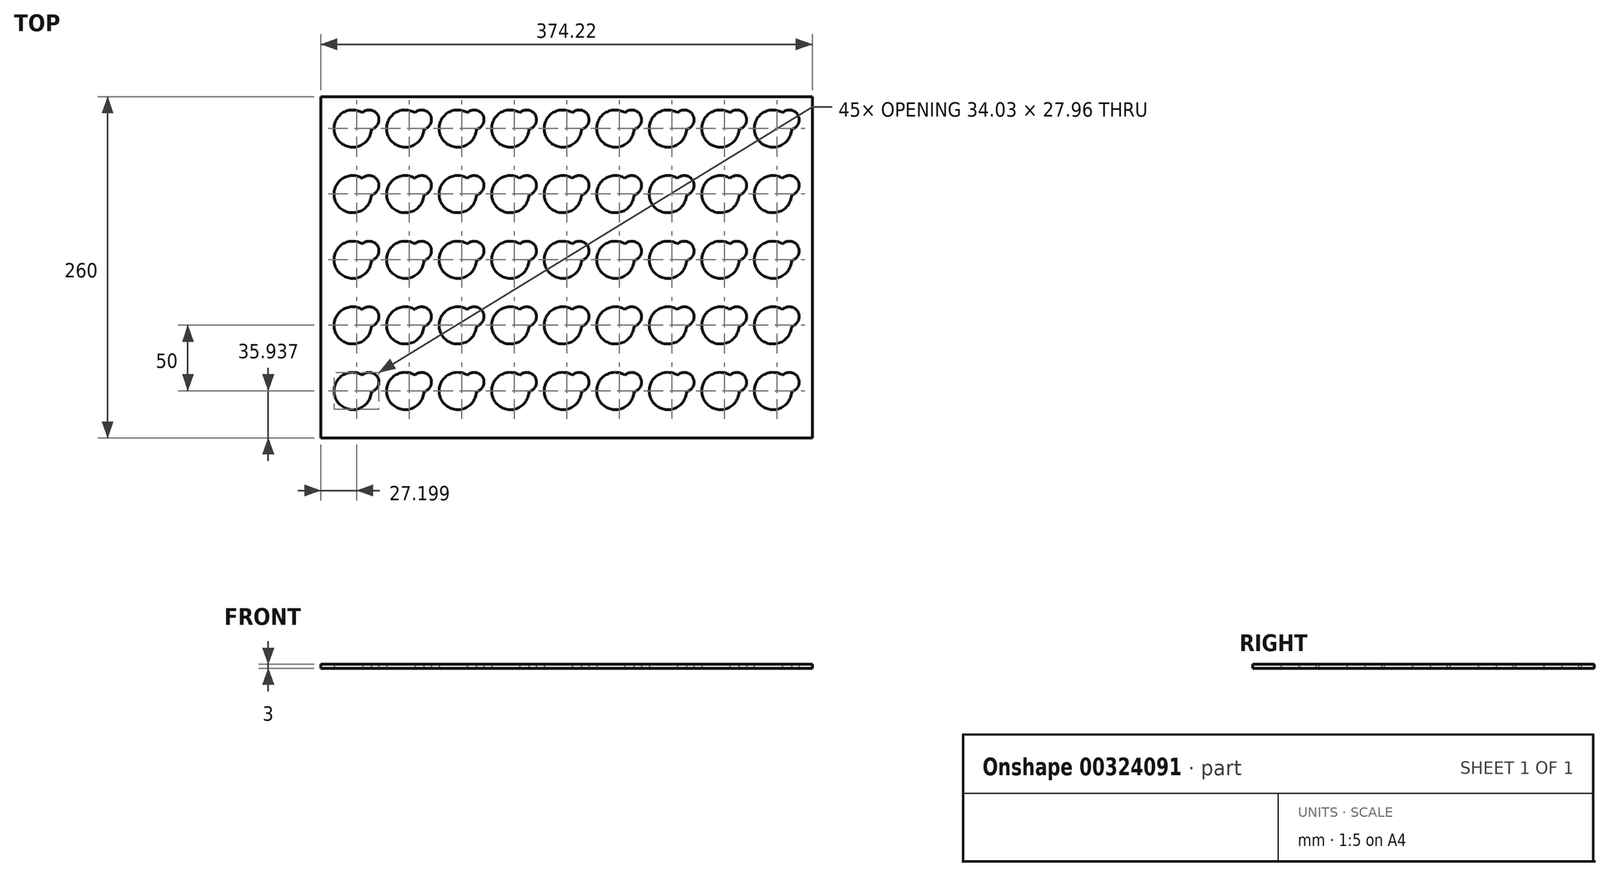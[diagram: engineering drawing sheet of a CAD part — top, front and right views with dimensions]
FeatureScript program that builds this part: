
annotation { "Feature Type Name" : "Feature", "Feature Type Description" : "" }
export const myFeature = defineFeature(function(context is Context, id is Id, definition is map)
    precondition{}
    {
        {
            var Q0;
            Q0=qCreatedBy(makeId("Top.planeOp"),FACE);
            var sketch = newSketch(context, id + "F0", { "sketchPlane" : qUnion([Q0])});
            skArc(sketch, "E0", {"start": v(7.36, 12.14) * mm, "mid": v(-12.52, -6.7) * mm, "end": v(14.19, -0.61) * mm});
            skArc(sketch, "E1", {"start": v(14.19, -0.61) * mm, "mid": v(19.13, 10.24) * mm, "end": v(7.36, 12.14) * mm});
            skLineSegment(sketch, "E2", {"start": v(0, 14.2) * mm, "end": v(12.52, 14.2) * mm, "construction": true});
            skArc(sketch, "E3.0.1.0", {"start": v(7.36, -37.86) * mm, "mid": v(-12.52, -56.7) * mm, "end": v(14.19, -50.61) * mm});
            skArc(sketch, "E3.0.1.1", {"start": v(14.19, -50.61) * mm, "mid": v(19.13, -39.76) * mm, "end": v(7.36, -37.86) * mm});
            skArc(sketch, "E3.0.2.0", {"start": v(7.36, -87.86) * mm, "mid": v(-12.52, -106.7) * mm, "end": v(14.19, -100.61) * mm});
            skArc(sketch, "E3.0.2.1", {"start": v(14.19, -100.61) * mm, "mid": v(19.13, -89.76) * mm, "end": v(7.36, -87.86) * mm});
            skArc(sketch, "E3.0.3.0", {"start": v(7.36, -137.86) * mm, "mid": v(-12.52, -156.7) * mm, "end": v(14.19, -150.61) * mm});
            skArc(sketch, "E3.0.3.1", {"start": v(14.19, -150.61) * mm, "mid": v(19.13, -139.76) * mm, "end": v(7.36, -137.86) * mm});
            skArc(sketch, "E3.0.4.0", {"start": v(7.36, -187.86) * mm, "mid": v(-12.52, -206.7) * mm, "end": v(14.19, -200.61) * mm});
            skArc(sketch, "E3.0.4.1", {"start": v(14.19, -200.61) * mm, "mid": v(19.13, -189.76) * mm, "end": v(7.36, -187.86) * mm});
            skArc(sketch, "E3.1.0.0", {"start": v(47.36, 12.14) * mm, "mid": v(27.48, -6.7) * mm, "end": v(54.19, -0.61) * mm});
            skArc(sketch, "E3.1.0.1", {"start": v(54.19, -0.61) * mm, "mid": v(59.13, 10.24) * mm, "end": v(47.36, 12.14) * mm});
            skArc(sketch, "E3.1.1.0", {"start": v(47.36, -37.86) * mm, "mid": v(27.48, -56.7) * mm, "end": v(54.19, -50.61) * mm});
            skArc(sketch, "E3.1.1.1", {"start": v(54.19, -50.61) * mm, "mid": v(59.13, -39.76) * mm, "end": v(47.36, -37.86) * mm});
            skArc(sketch, "E3.1.2.0", {"start": v(47.36, -87.86) * mm, "mid": v(27.48, -106.7) * mm, "end": v(54.19, -100.61) * mm});
            skArc(sketch, "E3.1.2.1", {"start": v(54.19, -100.61) * mm, "mid": v(59.13, -89.76) * mm, "end": v(47.36, -87.86) * mm});
            skArc(sketch, "E3.1.3.0", {"start": v(47.36, -137.86) * mm, "mid": v(27.48, -156.7) * mm, "end": v(54.19, -150.61) * mm});
            skArc(sketch, "E3.1.3.1", {"start": v(54.19, -150.61) * mm, "mid": v(59.13, -139.76) * mm, "end": v(47.36, -137.86) * mm});
            skArc(sketch, "E3.1.4.0", {"start": v(47.36, -187.86) * mm, "mid": v(27.48, -206.7) * mm, "end": v(54.19, -200.61) * mm});
            skArc(sketch, "E3.1.4.1", {"start": v(54.19, -200.61) * mm, "mid": v(59.13, -189.76) * mm, "end": v(47.36, -187.86) * mm});
            skArc(sketch, "E3.2.0.0", {"start": v(87.36, 12.14) * mm, "mid": v(67.48, -6.7) * mm, "end": v(94.19, -0.61) * mm});
            skArc(sketch, "E3.2.0.1", {"start": v(94.19, -0.61) * mm, "mid": v(99.13, 10.24) * mm, "end": v(87.36, 12.14) * mm});
            skArc(sketch, "E3.2.1.0", {"start": v(87.36, -37.86) * mm, "mid": v(67.48, -56.7) * mm, "end": v(94.19, -50.61) * mm});
            skArc(sketch, "E3.2.1.1", {"start": v(94.19, -50.61) * mm, "mid": v(99.13, -39.76) * mm, "end": v(87.36, -37.86) * mm});
            skArc(sketch, "E3.2.2.0", {"start": v(87.36, -87.86) * mm, "mid": v(67.48, -106.7) * mm, "end": v(94.19, -100.61) * mm});
            skArc(sketch, "E3.2.2.1", {"start": v(94.19, -100.61) * mm, "mid": v(99.13, -89.76) * mm, "end": v(87.36, -87.86) * mm});
            skArc(sketch, "E3.2.3.0", {"start": v(87.36, -137.86) * mm, "mid": v(67.48, -156.7) * mm, "end": v(94.19, -150.61) * mm});
            skArc(sketch, "E3.2.3.1", {"start": v(94.19, -150.61) * mm, "mid": v(99.13, -139.76) * mm, "end": v(87.36, -137.86) * mm});
            skArc(sketch, "E3.2.4.0", {"start": v(87.36, -187.86) * mm, "mid": v(67.48, -206.7) * mm, "end": v(94.19, -200.61) * mm});
            skArc(sketch, "E3.2.4.1", {"start": v(94.19, -200.61) * mm, "mid": v(99.13, -189.76) * mm, "end": v(87.36, -187.86) * mm});
            skArc(sketch, "E3.3.0.0", {"start": v(127.36, 12.14) * mm, "mid": v(107.48, -6.7) * mm, "end": v(134.19, -0.61) * mm});
            skArc(sketch, "E3.3.0.1", {"start": v(134.19, -0.61) * mm, "mid": v(139.13, 10.24) * mm, "end": v(127.36, 12.14) * mm});
            skArc(sketch, "E3.3.1.0", {"start": v(127.36, -37.86) * mm, "mid": v(107.48, -56.7) * mm, "end": v(134.19, -50.61) * mm});
            skArc(sketch, "E3.3.1.1", {"start": v(134.19, -50.61) * mm, "mid": v(139.13, -39.76) * mm, "end": v(127.36, -37.86) * mm});
            skArc(sketch, "E3.3.2.0", {"start": v(127.36, -87.86) * mm, "mid": v(107.48, -106.7) * mm, "end": v(134.19, -100.61) * mm});
            skArc(sketch, "E3.3.2.1", {"start": v(134.19, -100.61) * mm, "mid": v(139.13, -89.76) * mm, "end": v(127.36, -87.86) * mm});
            skArc(sketch, "E3.3.3.0", {"start": v(127.36, -137.86) * mm, "mid": v(107.48, -156.7) * mm, "end": v(134.19, -150.61) * mm});
            skArc(sketch, "E3.3.3.1", {"start": v(134.19, -150.61) * mm, "mid": v(139.13, -139.76) * mm, "end": v(127.36, -137.86) * mm});
            skArc(sketch, "E3.3.4.0", {"start": v(127.36, -187.86) * mm, "mid": v(107.48, -206.7) * mm, "end": v(134.19, -200.61) * mm});
            skArc(sketch, "E3.3.4.1", {"start": v(134.19, -200.61) * mm, "mid": v(139.13, -189.76) * mm, "end": v(127.36, -187.86) * mm});
            skArc(sketch, "E3.4.0.0", {"start": v(167.36, 12.14) * mm, "mid": v(147.48, -6.7) * mm, "end": v(174.19, -0.61) * mm});
            skArc(sketch, "E3.4.0.1", {"start": v(174.19, -0.61) * mm, "mid": v(179.13, 10.24) * mm, "end": v(167.36, 12.14) * mm});
            skArc(sketch, "E3.4.1.0", {"start": v(167.36, -37.86) * mm, "mid": v(147.48, -56.7) * mm, "end": v(174.19, -50.61) * mm});
            skArc(sketch, "E3.4.1.1", {"start": v(174.19, -50.61) * mm, "mid": v(179.13, -39.76) * mm, "end": v(167.36, -37.86) * mm});
            skArc(sketch, "E3.4.2.0", {"start": v(167.36, -87.86) * mm, "mid": v(147.48, -106.7) * mm, "end": v(174.19, -100.61) * mm});
            skArc(sketch, "E3.4.2.1", {"start": v(174.19, -100.61) * mm, "mid": v(179.13, -89.76) * mm, "end": v(167.36, -87.86) * mm});
            skArc(sketch, "E3.4.3.0", {"start": v(167.36, -137.86) * mm, "mid": v(147.48, -156.7) * mm, "end": v(174.19, -150.61) * mm});
            skArc(sketch, "E3.4.3.1", {"start": v(174.19, -150.61) * mm, "mid": v(179.13, -139.76) * mm, "end": v(167.36, -137.86) * mm});
            skArc(sketch, "E3.4.4.0", {"start": v(167.36, -187.86) * mm, "mid": v(147.48, -206.7) * mm, "end": v(174.19, -200.61) * mm});
            skArc(sketch, "E3.4.4.1", {"start": v(174.19, -200.61) * mm, "mid": v(179.13, -189.76) * mm, "end": v(167.36, -187.86) * mm});
            skArc(sketch, "E3.5.0.0", {"start": v(207.36, 12.14) * mm, "mid": v(187.48, -6.7) * mm, "end": v(214.19, -0.61) * mm});
            skArc(sketch, "E3.5.0.1", {"start": v(214.19, -0.61) * mm, "mid": v(219.13, 10.24) * mm, "end": v(207.36, 12.14) * mm});
            skArc(sketch, "E3.5.1.0", {"start": v(207.36, -37.86) * mm, "mid": v(187.48, -56.7) * mm, "end": v(214.19, -50.61) * mm});
            skArc(sketch, "E3.5.1.1", {"start": v(214.19, -50.61) * mm, "mid": v(219.13, -39.76) * mm, "end": v(207.36, -37.86) * mm});
            skArc(sketch, "E3.5.2.0", {"start": v(207.36, -87.86) * mm, "mid": v(187.48, -106.7) * mm, "end": v(214.19, -100.61) * mm});
            skArc(sketch, "E3.5.2.1", {"start": v(214.19, -100.61) * mm, "mid": v(219.13, -89.76) * mm, "end": v(207.36, -87.86) * mm});
            skArc(sketch, "E3.5.3.0", {"start": v(207.36, -137.86) * mm, "mid": v(187.48, -156.7) * mm, "end": v(214.19, -150.61) * mm});
            skArc(sketch, "E3.5.3.1", {"start": v(214.19, -150.61) * mm, "mid": v(219.13, -139.76) * mm, "end": v(207.36, -137.86) * mm});
            skArc(sketch, "E3.5.4.0", {"start": v(207.36, -187.86) * mm, "mid": v(187.48, -206.7) * mm, "end": v(214.19, -200.61) * mm});
            skArc(sketch, "E3.5.4.1", {"start": v(214.19, -200.61) * mm, "mid": v(219.13, -189.76) * mm, "end": v(207.36, -187.86) * mm});
            skArc(sketch, "E3.6.0.0", {"start": v(247.36, 12.14) * mm, "mid": v(227.48, -6.7) * mm, "end": v(254.19, -0.61) * mm});
            skArc(sketch, "E3.6.0.1", {"start": v(254.19, -0.61) * mm, "mid": v(259.13, 10.24) * mm, "end": v(247.36, 12.14) * mm});
            skArc(sketch, "E3.6.1.0", {"start": v(247.36, -37.86) * mm, "mid": v(227.48, -56.7) * mm, "end": v(254.19, -50.61) * mm});
            skArc(sketch, "E3.6.1.1", {"start": v(254.19, -50.61) * mm, "mid": v(259.13, -39.76) * mm, "end": v(247.36, -37.86) * mm});
            skArc(sketch, "E3.6.2.0", {"start": v(247.36, -87.86) * mm, "mid": v(227.48, -106.7) * mm, "end": v(254.19, -100.61) * mm});
            skArc(sketch, "E3.6.2.1", {"start": v(254.19, -100.61) * mm, "mid": v(259.13, -89.76) * mm, "end": v(247.36, -87.86) * mm});
            skArc(sketch, "E3.6.3.0", {"start": v(247.36, -137.86) * mm, "mid": v(227.48, -156.7) * mm, "end": v(254.19, -150.61) * mm});
            skArc(sketch, "E3.6.3.1", {"start": v(254.19, -150.61) * mm, "mid": v(259.13, -139.76) * mm, "end": v(247.36, -137.86) * mm});
            skArc(sketch, "E3.6.4.0", {"start": v(247.36, -187.86) * mm, "mid": v(227.48, -206.7) * mm, "end": v(254.19, -200.61) * mm});
            skArc(sketch, "E3.6.4.1", {"start": v(254.19, -200.61) * mm, "mid": v(259.13, -189.76) * mm, "end": v(247.36, -187.86) * mm});
            skArc(sketch, "E3.7.0.0", {"start": v(287.36, 12.14) * mm, "mid": v(267.48, -6.7) * mm, "end": v(294.19, -0.61) * mm});
            skArc(sketch, "E3.7.0.1", {"start": v(294.19, -0.61) * mm, "mid": v(299.13, 10.24) * mm, "end": v(287.36, 12.14) * mm});
            skArc(sketch, "E3.7.1.0", {"start": v(287.36, -37.86) * mm, "mid": v(267.48, -56.7) * mm, "end": v(294.19, -50.61) * mm});
            skArc(sketch, "E3.7.1.1", {"start": v(294.19, -50.61) * mm, "mid": v(299.13, -39.76) * mm, "end": v(287.36, -37.86) * mm});
            skArc(sketch, "E3.7.2.0", {"start": v(287.36, -87.86) * mm, "mid": v(267.48, -106.7) * mm, "end": v(294.19, -100.61) * mm});
            skArc(sketch, "E3.7.2.1", {"start": v(294.19, -100.61) * mm, "mid": v(299.13, -89.76) * mm, "end": v(287.36, -87.86) * mm});
            skArc(sketch, "E3.7.3.0", {"start": v(287.36, -137.86) * mm, "mid": v(267.48, -156.7) * mm, "end": v(294.19, -150.61) * mm});
            skArc(sketch, "E3.7.3.1", {"start": v(294.19, -150.61) * mm, "mid": v(299.13, -139.76) * mm, "end": v(287.36, -137.86) * mm});
            skArc(sketch, "E3.7.4.0", {"start": v(287.36, -187.86) * mm, "mid": v(267.48, -206.7) * mm, "end": v(294.19, -200.61) * mm});
            skArc(sketch, "E3.7.4.1", {"start": v(294.19, -200.61) * mm, "mid": v(299.13, -189.76) * mm, "end": v(287.36, -187.86) * mm});
            skArc(sketch, "E3.8.0.0", {"start": v(327.36, 12.14) * mm, "mid": v(307.48, -6.7) * mm, "end": v(334.19, -0.61) * mm});
            skArc(sketch, "E3.8.0.1", {"start": v(334.19, -0.61) * mm, "mid": v(339.13, 10.24) * mm, "end": v(327.36, 12.14) * mm});
            skArc(sketch, "E3.8.1.0", {"start": v(327.36, -37.86) * mm, "mid": v(307.48, -56.7) * mm, "end": v(334.19, -50.61) * mm});
            skArc(sketch, "E3.8.1.1", {"start": v(334.19, -50.61) * mm, "mid": v(339.13, -39.76) * mm, "end": v(327.36, -37.86) * mm});
            skArc(sketch, "E3.8.2.0", {"start": v(327.36, -87.86) * mm, "mid": v(307.48, -106.7) * mm, "end": v(334.19, -100.61) * mm});
            skArc(sketch, "E3.8.2.1", {"start": v(334.19, -100.61) * mm, "mid": v(339.13, -89.76) * mm, "end": v(327.36, -87.86) * mm});
            skArc(sketch, "E3.8.3.0", {"start": v(327.36, -137.86) * mm, "mid": v(307.48, -156.7) * mm, "end": v(334.19, -150.61) * mm});
            skArc(sketch, "E3.8.3.1", {"start": v(334.19, -150.61) * mm, "mid": v(339.13, -139.76) * mm, "end": v(327.36, -137.86) * mm});
            skArc(sketch, "E3.8.4.0", {"start": v(327.36, -187.86) * mm, "mid": v(307.48, -206.7) * mm, "end": v(334.19, -200.61) * mm});
            skArc(sketch, "E3.8.4.1", {"start": v(334.19, -200.61) * mm, "mid": v(339.13, -189.76) * mm, "end": v(327.36, -187.86) * mm});
            skLineSegment(sketch, "E3.direction1", {"start": v(0, 0) * mm, "end": v(40, 0) * mm, "construction": true});
            skLineSegment(sketch, "E3.direction2", {"start": v(0, 0) * mm, "end": v(0, -50) * mm, "construction": true});
            skPoint(sketch, "E4", {"position": v(-14.2, 0) * mm});
            skLineSegment(sketch, "E5", {"start": v(0, 14.2) * mm, "end": v(-14.2, 14.2) * mm, "construction": true});
            skLineSegment(sketch, "E6", {"start": v(-14.2, 14.2) * mm, "end": v(-24.2, 14.2) * mm, "construction": true});
            skLineSegment(sketch, "E7", {"start": v(-24.2, 14.2) * mm, "end": v(-24.2, 24.2) * mm, "construction": true});
            skLineSegment(sketch, "E8", {"start": v(332.52, -193.3) * mm, "end": v(340.02, -193.3) * mm, "construction": true});
            skLineSegment(sketch, "E9", {"start": v(320, -214.2) * mm, "end": v(340.02, -214.2) * mm, "construction": true});
            skLineSegment(sketch, "E10", {"start": v(340.02, -214.2) * mm, "end": v(350.02, -214.2) * mm, "construction": true});
            skLineSegment(sketch, "E11", {"start": v(350.02, -214.2) * mm, "end": v(350.02, -235.8) * mm, "construction": true});
            skLineSegment(sketch, "E12", {"start": v(340.02, -193.3) * mm, "end": v(340.02, -214.2) * mm, "construction": true});
            skLineSegment(sketch, "E13.bottom", {"start": v(-24.2, 24.2) * mm, "end": v(350.02, 24.2) * mm});
            skLineSegment(sketch, "E13.top", {"start": v(-24.2, -235.8) * mm, "end": v(350.02, -235.8) * mm});
            skLineSegment(sketch, "E13.left", {"start": v(-24.2, 24.2) * mm, "end": v(-24.2, -235.8) * mm});
            skLineSegment(sketch, "E13.right", {"start": v(350.02, 24.2) * mm, "end": v(350.02, -235.8) * mm});
            skLineSegment(sketch, "E14.bottom", {"start": v(418.01, 24.2) * mm, "end": v(489.12, 24.2) * mm});
            skLineSegment(sketch, "E14.top", {"start": v(418.01, -235.8) * mm, "end": v(489.12, -235.8) * mm});
            skLineSegment(sketch, "E14.left", {"start": v(418.01, 24.2) * mm, "end": v(418.01, -235.8) * mm});
            skLineSegment(sketch, "E14.right", {"start": v(489.12, 24.2) * mm, "end": v(489.12, -235.8) * mm});
            skArc(sketch, "E15", {"start": v(458.49, 12.23) * mm, "mid": v(437.3, -4.35) * mm, "end": v(464.17, -5.64) * mm});
            skArc(sketch, "E16", {"start": v(464.17, -5.64) * mm, "mid": v(474.18, 7.38) * mm, "end": v(458.49, 12.23) * mm});
            skLineSegment(sketch, "E17", {"start": v(450.97, 14.35) * mm, "end": v(464.65, 14.35) * mm, "construction": true});
            skLineSegment(sketch, "E18.0.1.0", {"start": v(450.97, -25.6) * mm, "end": v(464.25, -25.6) * mm, "construction": true});
            skArc(sketch, "E18.0.1.1", {"start": v(458.46, -27.72) * mm, "mid": v(437.7, -45.2) * mm, "end": v(464.79, -43.58) * mm});
            skArc(sketch, "E18.0.1.2", {"start": v(464.79, -43.58) * mm, "mid": v(472.61, -31.26) * mm, "end": v(458.46, -27.72) * mm});
            skLineSegment(sketch, "E18.0.2.0", {"start": v(450.93, -65.62) * mm, "end": v(463.73, -65.62) * mm, "construction": true});
            skArc(sketch, "E18.0.2.1", {"start": v(458.35, -67.7) * mm, "mid": v(438.12, -86.12) * mm, "end": v(465.08, -81.5) * mm});
            skArc(sketch, "E18.0.2.2", {"start": v(465.08, -81.5) * mm, "mid": v(470.92, -70.11) * mm, "end": v(458.35, -67.7) * mm});
            skLineSegment(sketch, "E18.0.3.0", {"start": v(450.52, -106.04) * mm, "end": v(462.76, -106.04) * mm, "construction": true});
            skArc(sketch, "E18.0.3.1", {"start": v(457.83, -108.06) * mm, "mid": v(438.28, -127.44) * mm, "end": v(464.71, -119.76) * mm});
            skArc(sketch, "E18.0.3.2", {"start": v(464.71, -119.76) * mm, "mid": v(468.8, -109.49) * mm, "end": v(457.83, -108.06) * mm});
            skLineSegment(sketch, "E18.0.4.0", {"start": v(450.97, -145.9) * mm, "end": v(462.54, -145.9) * mm, "construction": true});
            skArc(sketch, "E18.0.4.1", {"start": v(458.12, -147.84) * mm, "mid": v(439.4, -168.2) * mm, "end": v(464.88, -157.43) * mm});
            skArc(sketch, "E18.0.4.2", {"start": v(464.88, -157.43) * mm, "mid": v(467.44, -148.44) * mm, "end": v(458.12, -147.84) * mm});
            skLineSegment(sketch, "E18.0.5.0", {"start": v(450.97, -186) * mm, "end": v(461.74, -186) * mm, "construction": true});
            skArc(sketch, "E18.0.5.1", {"start": v(457.89, -187.81) * mm, "mid": v(440.2, -209.2) * mm, "end": v(464.24, -195.33) * mm});
            skArc(sketch, "E18.0.5.2", {"start": v(464.24, -195.33) * mm, "mid": v(465.56, -187.77) * mm, "end": v(457.89, -187.81) * mm});
            skCircle(sketch, "E19", {"center": v(450.97, -39.9) * mm, "radius": 14.3 * mm});
            skCircle(sketch, "E20", {"center": v(450.97, 0) * mm, "radius": 14.35 * mm});
            skCircle(sketch, "E21", {"center": v(450.93, -79.87) * mm, "radius": 14.25 * mm});
            skCircle(sketch, "E22", {"center": v(450.52, -120.24) * mm, "radius": 14.2 * mm});
            skCircle(sketch, "E23", {"center": v(450.97, -160.05) * mm, "radius": 14.15 * mm});
            skCircle(sketch, "E24", {"center": v(450.97, -200.1) * mm, "radius": 14.1 * mm});
            skLineSegment(sketch, "E25", {"start": v(80, 0) * mm, "end": v(80, -14.2) * mm, "construction": true});
            skLineSegment(sketch, "E26", {"start": v(80, -14.2) * mm, "end": v(80, -35.8) * mm, "construction": true});
            skLineSegment(sketch, "E27", {"start": v(80, -35.8) * mm, "end": v(80, -50) * mm, "construction": true});
            skSolve(sketch);
        }
        {
            var Q0;
            Q0=makeQuery(id+"F0.imprint","IMPRINT",FACE,{"disambiguationData":[TD([[makeQuery(id+"F0.imprint","IMPRINT",EDGE,{"derivedFrom":sQuery(id+"F0.wireOp",EDGE,"E0")}),-1.0]])]});
            extrude(context, id + "F1", {"entities" : qUnion([Q0]), "depth" : 3 * mm});
        }
    });
